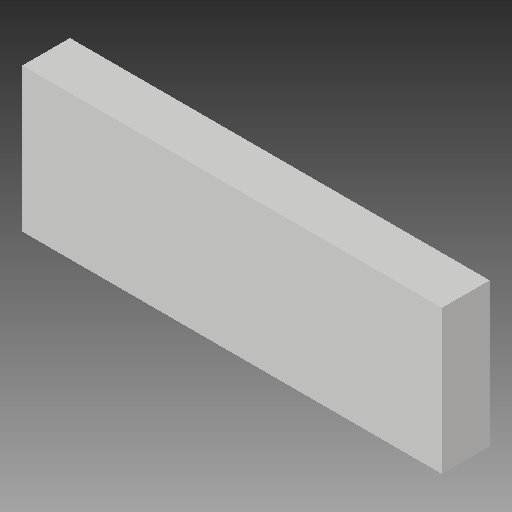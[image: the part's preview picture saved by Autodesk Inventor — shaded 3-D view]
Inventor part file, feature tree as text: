
AUTODESK INVENTOR PART (.ipt)
format: ipt  version: 2018 (Build 220112000, 112)  size: 90,624 bytes
history: native  units: mm
features: other x1, extrude x1, sketch x1
ambient origin geometry x8: Origin, YZ Plane, XZ Plane, XY Plane, X Axis, Y Axis, Z Axis, Center Point
bodies: Body1 (feature_tree)
feature tree (3):
  other  "Sólido1"
  extrude  "Extrusão1"  Depth=140.0mm
  sketch  "Esboço1"  dims[d10=15.88mm d11=0.0mm d13=140.0mm d14=48.0mm]
